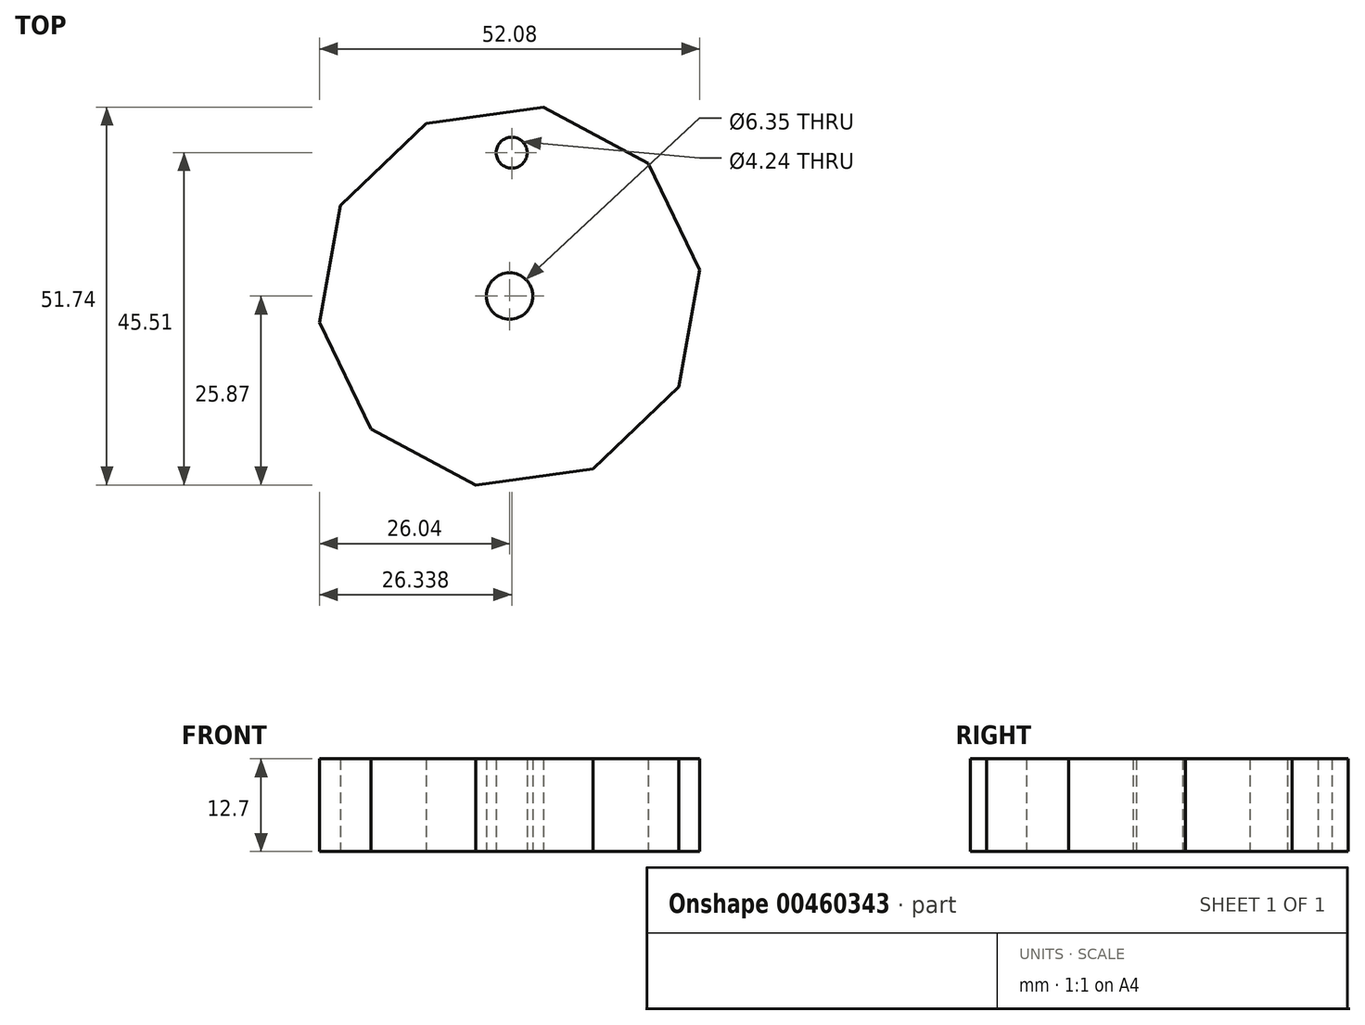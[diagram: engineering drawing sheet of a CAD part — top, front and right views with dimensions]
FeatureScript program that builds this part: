
annotation { "Feature Type Name" : "Feature", "Feature Type Description" : "" }
export const myFeature = defineFeature(function(context is Context, id is Id, definition is map)
    precondition{}
    {
        {
            var Q0;
            Q0=qCreatedBy(makeId("Top.planeOp"),FACE);
            var sketch = newSketch(context, id + "F0", { "sketchPlane" : qUnion([Q0])});
            skCircle(sketch, "E0", {"center": v(-35.5, 0) * mm, "radius": 3.17 * mm});
            skCircle(sketch, "E1.cCircle", {"center": v(-35.5, 0) * mm, "radius": 25 * mm, "construction": true});
            skLineSegment(sketch, "E1.0", {"start": v(-16.54, 18.2) * mm, "end": v(-9.46, 3.58) * mm});
            skLineSegment(sketch, "E1.1", {"start": v(-9.46, 3.58) * mm, "end": v(-12.33, -12.41) * mm});
            skLineSegment(sketch, "E1.2", {"start": v(-12.33, -12.41) * mm, "end": v(-24.05, -23.66) * mm});
            skLineSegment(sketch, "E1.3", {"start": v(-24.05, -23.66) * mm, "end": v(-40.14, -25.87) * mm});
            skLineSegment(sketch, "E1.4", {"start": v(-40.14, -25.87) * mm, "end": v(-54.46, -18.2) * mm});
            skLineSegment(sketch, "E1.5", {"start": v(-54.46, -18.2) * mm, "end": v(-61.54, -3.58) * mm});
            skLineSegment(sketch, "E1.6", {"start": v(-61.54, -3.58) * mm, "end": v(-58.67, 12.41) * mm});
            skLineSegment(sketch, "E1.7", {"start": v(-58.67, 12.41) * mm, "end": v(-46.95, 23.66) * mm});
            skLineSegment(sketch, "E1.8", {"start": v(-46.95, 23.66) * mm, "end": v(-30.86, 25.87) * mm});
            skLineSegment(sketch, "E1.9", {"start": v(-30.86, 25.87) * mm, "end": v(-16.54, 18.2) * mm});
            skPoint(sketch, "E1.0.midPoint", {"position": v(-13, 10.9) * mm});
            skCircle(sketch, "E2", {"center": v(-35.2, 19.64) * mm, "radius": 2.12 * mm});
            skSolve(sketch);
        }
        {
            var Q0;
            Q0=qSketchRegion(id+"F0",true);
            extrude(context, id + "F1", {"entities" : qUnion([Q0]), "depth" : 12.7 * mm});
        }
    });
